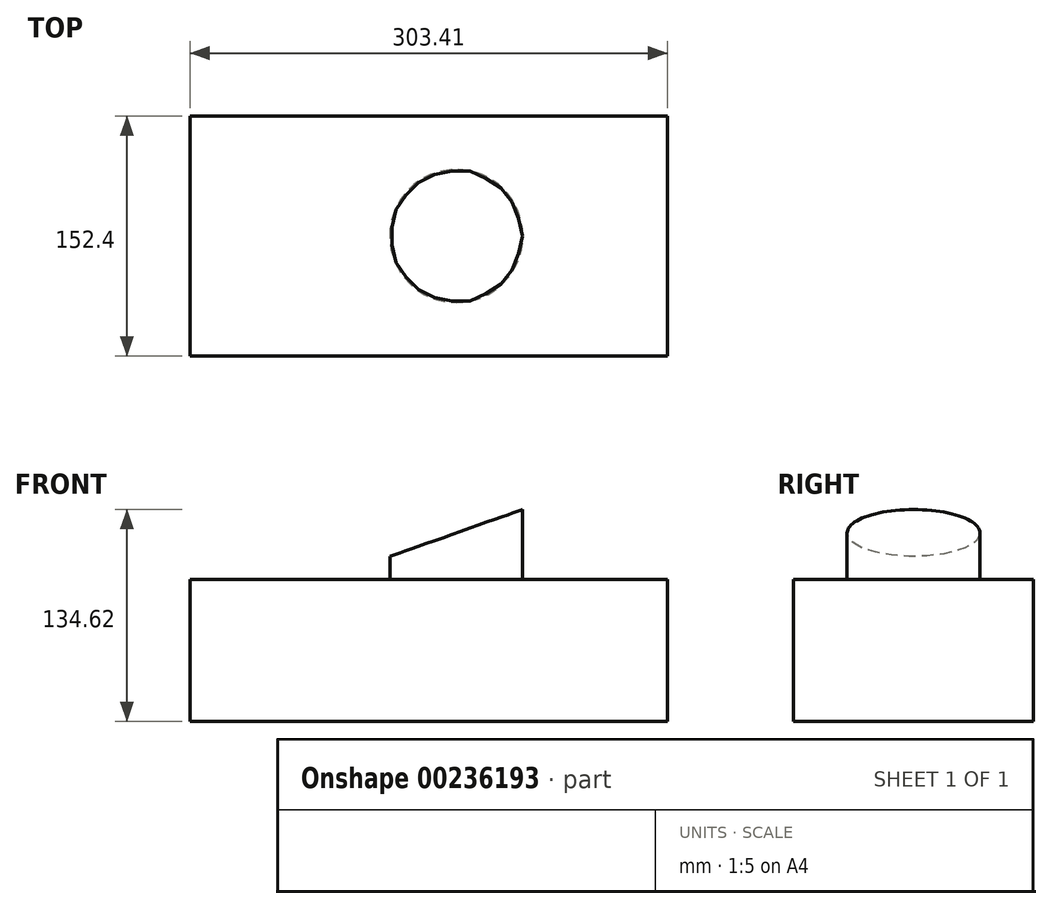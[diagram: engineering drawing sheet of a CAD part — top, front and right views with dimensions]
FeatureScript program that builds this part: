
annotation { "Feature Type Name" : "Feature", "Feature Type Description" : "" }
export const myFeature = defineFeature(function(context is Context, id is Id, definition is map)
    precondition{}
    {
        {
            var Q0;
            Q0=qCreatedBy(makeId("Front.planeOp"),FACE);
            var sketch = newSketch(context, id + "F0", { "sketchPlane" : qUnion([Q0])});
            skLineSegment(sketch, "E0.bottom", {"start": v(-154.31, 30.75) * mm, "end": v(149.1, 30.75) * mm});
            skLineSegment(sketch, "E0.top", {"start": v(-154.31, -59.3) * mm, "end": v(149.1, -59.3) * mm});
            skLineSegment(sketch, "E0.left", {"start": v(-154.31, 30.75) * mm, "end": v(-154.31, -59.3) * mm});
            skLineSegment(sketch, "E0.right", {"start": v(149.1, 30.75) * mm, "end": v(149.1, -59.3) * mm});
            skSolve(sketch);
        }
        {
            var Q0;
            Q0=qCreatedBy(makeId("Front.planeOp"),FACE);
            var sketch = newSketch(context, id + "F1", { "sketchPlane" : qUnion([Q0])});
            skLineSegment(sketch, "E1.bottom", {"start": v(-28.18, 76.35) * mm, "end": v(57.06, 76.35) * mm});
            skLineSegment(sketch, "E1.top", {"start": v(-28.18, -54.48) * mm, "end": v(57.06, -54.48) * mm});
            skLineSegment(sketch, "E1.left", {"start": v(-28.18, 76.35) * mm, "end": v(-28.18, -54.48) * mm});
            skLineSegment(sketch, "E1.right", {"start": v(57.06, 76.35) * mm, "end": v(57.06, -54.48) * mm});
            skLineSegment(sketch, "E2", {"start": v(-28.18, 47.8) * mm, "end": v(57.06, 76.35) * mm});
            skLineSegment(sketch, "E3", {"start": v(14.86, 76.35) * mm, "end": v(14.86, -54.48) * mm});
            skSolve(sketch);
        }
        {
            var Q0;
            Q0=makeQuery(id+"F0.imprint","IMPRINT",FACE,{"disambiguationData":[TD([[makeQuery(id+"F0.imprint","IMPRINT",EDGE,{"derivedFrom":sQuery(id+"F0.wireOp",EDGE,"E0.bottom")}),-1.0]])]});
            extrude(context, id + "F2", {"entities" : qUnion([Q0]), "depth" : 76.2 * mm, "hasSecondDirection" : true, "secondDirectionOppositeDirection" : true, "secondDirectionDepth" : 76.2 * mm});
        }
        {
            var Q0;
            {var subQ0=sQuery(id+"F1.wireOp",EDGE,"E1.right");Q0=makeQuery(id+"F1.imprint","IMPRINT",FACE,{"disambiguationData":[TD([[makeQuery(id+"F1.imprint","IMPRINT",EDGE,{"derivedFrom":subQ0}),-1.0]])]});}
            var Q1;
            {var subQ1=sQuery(id+"F1.wireOp",EDGE,"E1.bottom");var subQ3=sQuery(id+"F1.wireOp",EDGE,"E3");var subQ4=makeQuery(id+"F1.imprint","INTERSECT",VERTEX,{"derivedFrom":[subQ1,subQ3]});Q1=makeQuery(id+"F1.imprint","IMPRINT",FACE,{"disambiguationData":[TD([[makeQuery(id+"F1.imprint","IMPRINT",EDGE,{"disambiguationData":[TD([[subQ4,-1.0]])],"derivedFrom":subQ3}),1.0]])]});}
            var Q2;
            Q2=sQuery(id+"F1.wireOp",EDGE,"E3");
            revolve(context, id + "F3", {"operationType" : NewBodyOperationType.ADD, "entities" : qUnion([Q0, Q1]), "axis" : qUnion([Q2]), "revolveType" : RevolveType.FULL});
        }
        {
            var Q0;
            Q0=qCreatedBy(makeId("Front.planeOp"),FACE);
            var sketch = newSketch(context, id + "F4", { "sketchPlane" : qUnion([Q0])});
            skLineSegment(sketch, "E4", {"start": v(70.52, 80.07) * mm, "end": v(-45.77, 39.02) * mm});
            skLineSegment(sketch, "E5", {"start": v(-45.77, 39.02) * mm, "end": v(-45.77, 80.32) * mm});
            skLineSegment(sketch, "E6", {"start": v(-45.77, 80.32) * mm, "end": v(70.52, 80.07) * mm});
            skSolve(sketch);
        }
        {
            var Q0;
            Q0=makeQuery(id+"F4.imprint","IMPRINT",FACE,{"disambiguationData":[TD([[makeQuery(id+"F4.imprint","IMPRINT",EDGE,{"derivedFrom":sQuery(id+"F4.wireOp",EDGE,"E4")}),-1.0]])]});
            extrude(context, id + "F5", {"entities" : qUnion([Q0]), "operationType" : NewBodyOperationType.REMOVE, "oppositeDirection" : true, "depth" : 50.8 * mm, "hasSecondDirection" : true, "secondDirectionOppositeDirection" : false, "secondDirectionDepth" : 50.8 * mm});
        }
    });
